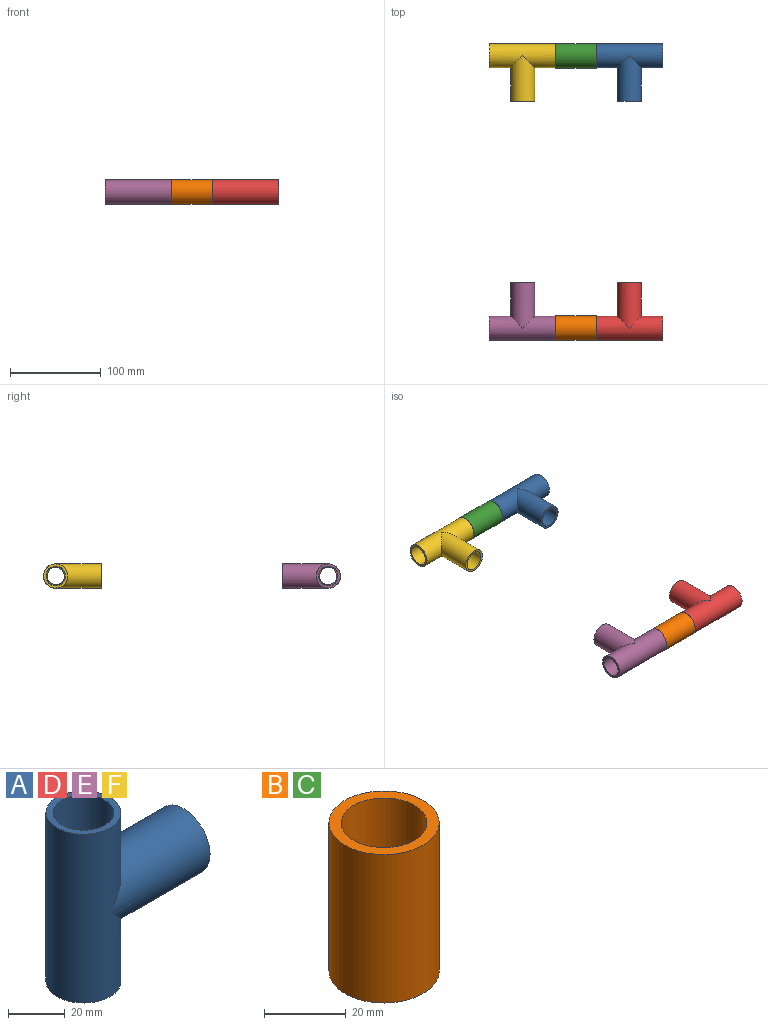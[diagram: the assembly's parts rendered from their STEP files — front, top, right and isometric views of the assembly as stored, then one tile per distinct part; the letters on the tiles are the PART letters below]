
ASSEMBLY  parts=6 mates=11
PART A: 7 faces, bbox 63.3x26.5x73 mm
  f0: cylinder r=10.75mm len=73mm, axis (0,0,-1), area 4468.5mm2, adj f2,f3,f6
  f1: cylinder r=13.25mm len=73mm, axis (0,0,-1), area 5375.2mm2, adj f2,f3,f5
  f2: plane 26.5x26.5mm, normal (0,0,1), area 188.5mm2, adj f0,f1
  f3: plane 26.5x26.5mm, normal (0,0,-1), area 188.5mm2, adj f0,f1
  f4: plane 26.5x26.5mm, normal (1,0,0), area 188.5mm2, adj f5,f6
  f5: cylinder r=13.25mm len=50mm, axis (1,0,0), area 3460.4mm2, adj f1,f4
  f6: cylinder r=10.75mm len=50mm, axis (1,0,0), area 2915mm2, adj f0,f4
PART B: 8 faces, bbox 27x27x44.5 mm
  f0: cylinder r=10.5mm len=21mm, axis (0,0,-1), area 1385.4mm2, adj f4,f7
  f1: cylinder r=10.5mm len=21mm, axis (0,0,-1), area 1385.4mm2, adj f3,f6
  f2: cylinder r=13.5mm len=44.5mm, axis (0,0,-1), area 3774.6mm2, adj f3,f4
  f3: plane 27x27mm, normal (0,0,1), area 226.2mm2, adj f1,f2
  f4: plane 27x27mm, normal (0,0,-1), area 226.2mm2, adj f0,f2
  f5: cylinder r=9.5mm len=19mm, axis (0,0,-1), area 149.2mm2, adj f6,f7
  f6: plane 21x21mm, normal (0,0,1), area 62.8mm2, adj f1,f5
  f7: plane 21x21mm, normal (0,0,-1), area 62.8mm2, adj f0,f5
PART C: same geometry as B
PART D: same geometry as A
PART E: same geometry as A
PART F: same geometry as A
PLACE A rot(axis=(-0.58,0.58,-0.58),120deg) t=(72.66,268.54,24.78)mm
PLACE B rot(axis=(0,-1,0),90deg) t=(13.91,-31.46,24.78)mm
PLACE C rot(axis=(-0.06,-1,0.06),90.2deg) t=(13.91,268.54,24.78)mm
PLACE D rot(axis=(-0.58,-0.58,0.58),120deg) t=(72.66,-31.46,24.78)mm
PLACE E rot(axis=(0.58,0.58,0.58),120deg) t=(-44.84,-31.46,24.78)mm fixed
PLACE F rot(axis=(-0.58,0.58,-0.58),120deg) t=(-44.84,268.54,24.78)mm
MATE cylindrical B.f2 <-> E.f1  axis (1,0,0) through (13.91,-31.46,24.78)mm
MATE cylindrical D.f5 <-> A.f5  axis (0,1,0) through (72.66,-6.61,24.78)mm
MATE cylindrical F.f1 <-> C.f2  axis (-1,0,0) through (-44.84,268.54,24.78)mm
MATE cylindrical C.f2 <-> A.f1  axis (1,0,0) through (13.91,268.54,24.78)mm
MATE planar D.f1 <-> B.f2  axis (-1,0,0) through (36.16,-31.46,24.78)mm
MATE cylindrical F.f5 <-> E.f5  axis (0,-1,0) through (-44.84,243.69,24.78)mm
MATE planar C.f2 <-> A.f1  axis (1,0,0) through (36.16,268.54,24.78)mm
MATE planar C.f2 <-> F.f1  axis (-1,0,0) through (-8.34,268.54,24.78)mm
MATE planar A.f5 <-> D.f5  axis (0,-1,0) through (72.66,218.54,24.78)mm
MATE planar E.f1 <-> B.f2  axis (1,0,0) through (-8.34,-31.46,24.78)mm
MATE cylindrical B.f2 <-> D.f1  axis (1,0,0) through (13.91,-31.46,24.78)mm
